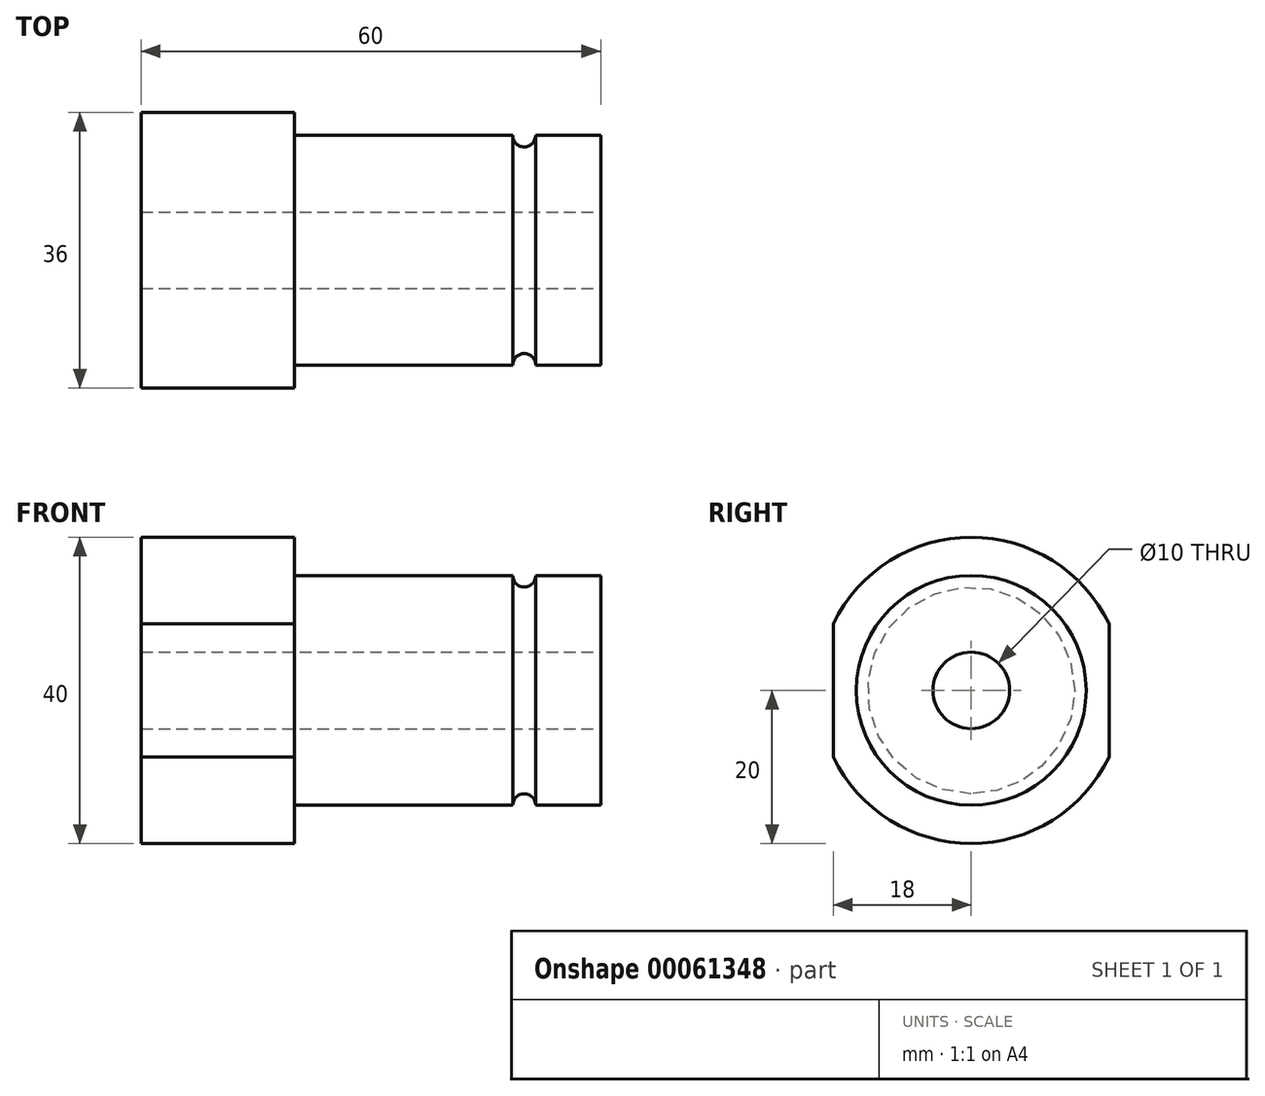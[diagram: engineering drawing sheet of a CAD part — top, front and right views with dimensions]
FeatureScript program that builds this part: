
annotation { "Feature Type Name" : "Feature", "Feature Type Description" : "" }
export const myFeature = defineFeature(function(context is Context, id is Id, definition is map)
    precondition{}
    {
        {
            var Q0;
            Q0=qCreatedBy(makeId("Right.planeOp"),FACE);
            var sketch = newSketch(context, id + "F0", { "sketchPlane" : qUnion([Q0])});
            skCircle(sketch, "E0", {"center": v(0, 0) * mm, "radius": 20 * mm});
            skSolve(sketch);
        }
        {
            var Q0;
            Q0=makeQuery(id+"F0.imprint","IMPRINT",FACE,{"disambiguationData":[TD([[makeQuery(id+"F0.imprint","IMPRINT",EDGE,{"derivedFrom":sQuery(id+"F0.wireOp",EDGE,"E0")}),1.0]])]});
            extrude(context, id + "F1", {"entities" : qUnion([Q0]), "depth" : 60 * mm});
        }
        {
            var Q0;
            Q0=makeQuery(id+"F1.opExtrude","CAP_FACE",FACE,{"disambiguationData":[OSD([sQuery(id+"F0.wireOp",EDGE,"E0")])],"isStart":false});
            var sketch = newSketch(context, id + "F2", { "sketchPlane" : qUnion([Q0])});
            skCircle(sketch, "E1", {"center": v(0, 0) * mm, "radius": 15 * mm});
            skSolve(sketch);
        }
        {
            var Q0;
            Q0=makeQuery(id+"F2.imprint","IMPRINT",FACE,{"disambiguationData":[TD([[makeQuery(id+"F2.imprint","IMPRINT",EDGE,{"derivedFrom":sQuery(id+"F2.wireOp",EDGE,"E1")}),-1.0]])]});
            extrude(context, id + "F3", {"entities" : qUnion([Q0]), "operationType" : NewBodyOperationType.REMOVE, "oppositeDirection" : true, "depth" : 40 * mm});
        }
        {
            var Q0;
            Q0=makeQuery(id+"F3.boolean.opBoolean","COPY",FACE,{"derivedFrom":makeQuery(id+"F3.opExtrude","CAP_FACE",FACE,{"disambiguationData":[OSD([sQuery(id+"F0.wireOp",EDGE,"E0"),sQuery(id+"F2.wireOp",EDGE,"E1")])],"isStart":false})});
            var sketch = newSketch(context, id + "F4", { "sketchPlane" : qUnion([Q0])});
            skArc(sketch, "E2", {"start": v(-18, 8.72) * mm, "mid": v(-20, 0) * mm, "end": v(-18, -8.72) * mm});
            skLineSegment(sketch, "E3.0", {"start": v(-18, 8.72) * mm, "end": v(-18, -8.72) * mm});
            skLineSegment(sketch, "E4.0", {"start": v(18, 8.72) * mm, "end": v(18, -8.72) * mm});
            skArc(sketch, "E5.trimOffspring", {"start": v(18, -8.72) * mm, "mid": v(20, 0) * mm, "end": v(18, 8.72) * mm});
            skSolve(sketch);
        }
        {
            var Q0;
            Q0 = qSketchRegion(id + "F4", true);
            extrude(context, id + "F5", {"entities" : qUnion([Q0]), "operationType" : NewBodyOperationType.REMOVE, "oppositeDirection" : true, "depth" : 20 * mm});
        }
        {
            var Q0;
            Q0=qCreatedBy(makeId("Front.planeOp"),FACE);
            var sketch = newSketch(context, id + "F6", { "sketchPlane" : qUnion([Q0])});
            skCircle(sketch, "E6", {"center": v(50, 15) * mm, "radius": 1.5 * mm});
            skLineSegment(sketch, "E7", {"start": v(66.54, 0) * mm, "end": v(-16, 0) * mm});
            skSolve(sketch);
        }
        {
            var Q0;
            Q0=makeQuery(id+"F6.imprint","IMPRINT",FACE,{"disambiguationData":[TD([[makeQuery(id+"F6.imprint","IMPRINT",EDGE,{"derivedFrom":sQuery(id+"F6.wireOp",EDGE,"E6")}),1.0]])]});
            var Q1;
            Q1=makeQuery(id+"F3.boolean.opBoolean","COPY",FACE,{"derivedFrom":makeQuery(id+"F3.opExtrude","SWEPT_FACE",FACE,{"disambiguationData":[OSD([sQuery(id+"F2.wireOp",EDGE,"E1")])]})});
            revolve(context, id + "F7", {"operationType" : NewBodyOperationType.REMOVE, "entities" : qUnion([Q0]), "axis" : qUnion([Q1]), "revolveType" : RevolveType.FULL, "oppositeDirection" : true});
        }
        {
            var Q0;
            Q0=makeQuery(id+"F1.opExtrude","CAP_FACE",FACE,{"disambiguationData":[OSD([sQuery(id+"F0.wireOp",EDGE,"E0")])],"isStart":false});
            var sketch = newSketch(context, id + "F8", { "sketchPlane" : qUnion([Q0])});
            skCircle(sketch, "E8", {"center": v(0, 0) * mm, "radius": 5 * mm});
            skSolve(sketch);
        }
        {
            var Q0;
            Q0=makeQuery(id+"F8.imprint","IMPRINT",FACE,{"disambiguationData":[TD([[makeQuery(id+"F8.imprint","IMPRINT",EDGE,{"derivedFrom":sQuery(id+"F8.wireOp",EDGE,"E8")}),1.0]])]});
            var Q1;
            Q1=sQuery(id+"F8.wireOp",EDGE,"E8");
            extrude(context, id + "F9", {"entities" : qUnion([Q0]), "operationType" : NewBodyOperationType.REMOVE, "surfaceEntities" : qUnion([Q1]), "oppositeDirection" : true, "depth" : 60 * mm});
        }
    });
